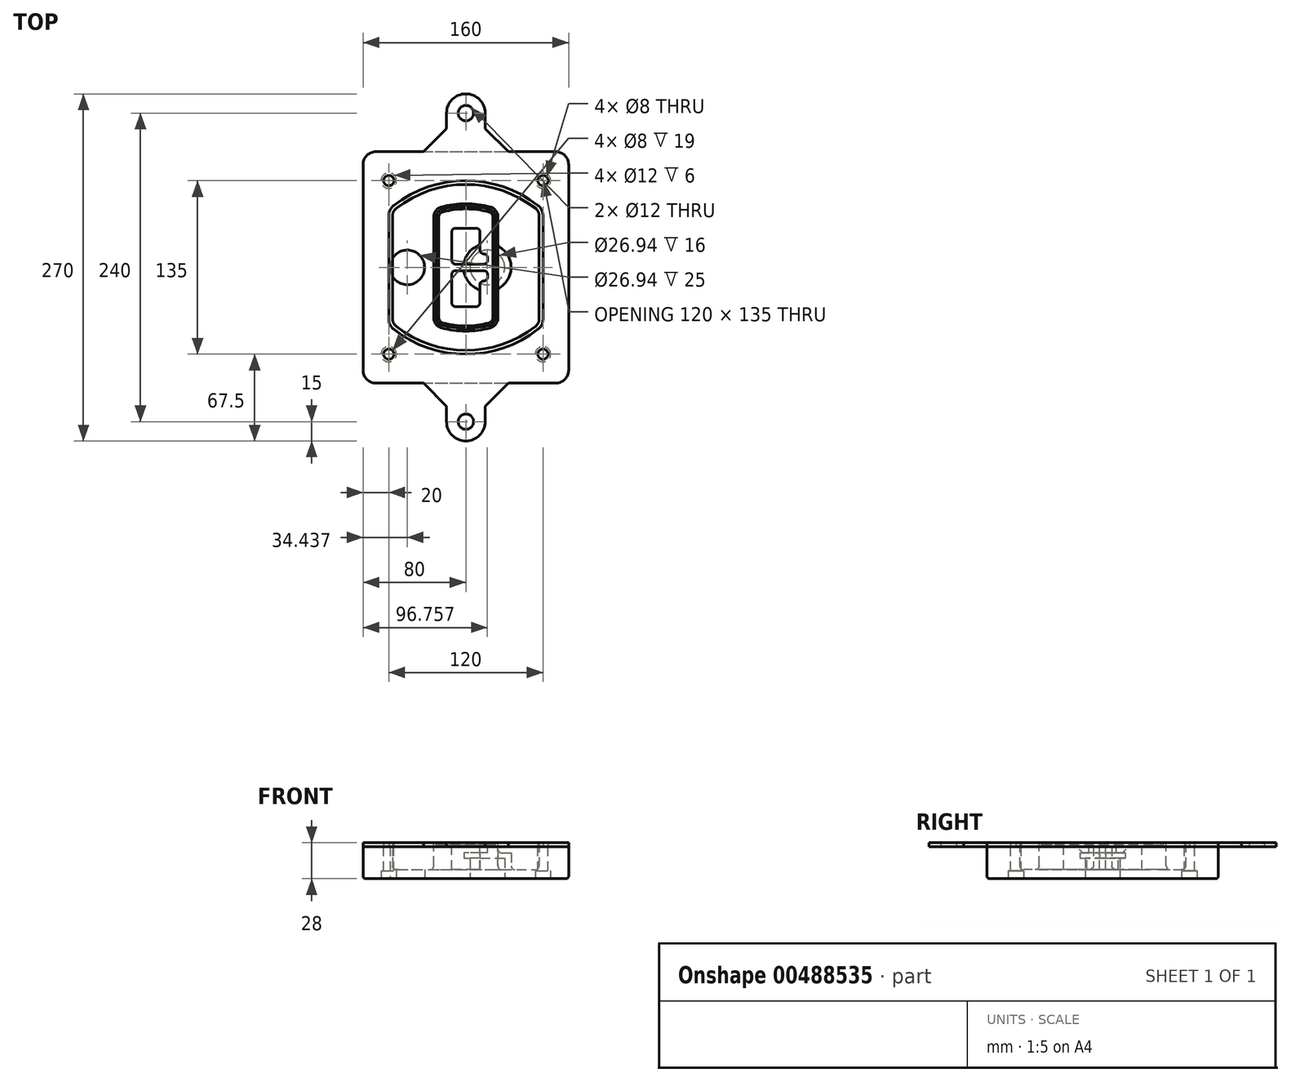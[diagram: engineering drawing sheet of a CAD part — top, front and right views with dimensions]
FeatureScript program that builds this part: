
annotation { "Feature Type Name" : "Feature", "Feature Type Description" : "" }
export const myFeature = defineFeature(function(context is Context, id is Id, definition is map)
    precondition{}
    {
        {
            var Q0;
            Q0=qCreatedBy(makeId("Top.planeOp"),FACE);
            var sketch = newSketch(context, id + "F0", { "sketchPlane" : qUnion([Q0])});
            skPoint(sketch, "E0.rect.middle", {"position": v(0, 0) * mm});
            skLineSegment(sketch, "E1.bottom", {"start": v(-70, -90) * mm, "end": v(70, -90) * mm});
            skLineSegment(sketch, "E1.top", {"start": v(-70, 90) * mm, "end": v(70, 90) * mm});
            skLineSegment(sketch, "E1.left", {"start": v(-80, -80) * mm, "end": v(-80, 80) * mm});
            skLineSegment(sketch, "E1.right", {"start": v(80, -80) * mm, "end": v(80, 80) * mm});
            skLineSegment(sketch, "E2", {"start": v(-80, 90) * mm, "end": v(80, -90) * mm, "construction": true});
            skLineSegment(sketch, "E3", {"start": v(80, 90) * mm, "end": v(-80, -90) * mm, "construction": true});
            skCircle(sketch, "E4", {"center": v(-60, 67.5) * mm, "radius": 4 * mm});
            skCircle(sketch, "E5", {"center": v(60, 67.5) * mm, "radius": 4 * mm});
            skCircle(sketch, "E6", {"center": v(60, -67.5) * mm, "radius": 4 * mm});
            skCircle(sketch, "E7", {"center": v(-60, -67.5) * mm, "radius": 4 * mm});
            skLineSegment(sketch, "E8", {"start": v(-60, 67.5) * mm, "end": v(60, 67.5) * mm, "construction": true});
            skLineSegment(sketch, "E9", {"start": v(60, 67.5) * mm, "end": v(60, -67.5) * mm, "construction": true});
            skLineSegment(sketch, "E10", {"start": v(60, -67.5) * mm, "end": v(-60, -67.5) * mm, "construction": true});
            skLineSegment(sketch, "E11", {"start": v(-60, -67.5) * mm, "end": v(-60, 67.5) * mm, "construction": true});
            skLineSegment(sketch, "E12", {"start": v(-60, 40.3) * mm, "end": v(-60, -40.3) * mm});
            skLineSegment(sketch, "E13", {"start": v(60, 40.3) * mm, "end": v(60, -40.3) * mm});
            skArc(sketch, "E14", {"start": v(56.15, 48.18) * mm, "mid": v(0, 67.5) * mm, "end": v(-56.15, 48.18) * mm});
            skArc(sketch, "E15", {"start": v(-56.15, -48.18) * mm, "mid": v(0, -67.5) * mm, "end": v(56.15, -48.18) * mm});
            skLineSegment(sketch, "E16", {"start": v(-60, 0) * mm, "end": v(60, 0) * mm, "construction": true});
            skPoint(sketch, "E17.visualSharp", {"position": v(-60, -45) * mm});
            skArc(sketch, "E17.filletArc", {"start": v(-60, -40.3) * mm, "mid": v(-58.99, -44.68) * mm, "end": v(-56.15, -48.18) * mm});
            skPoint(sketch, "E18.visualSharp", {"position": v(-60, 45) * mm});
            skArc(sketch, "E18.filletArc", {"start": v(-56.15, 48.18) * mm, "mid": v(-58.99, 44.68) * mm, "end": v(-60, 40.3) * mm});
            skPoint(sketch, "E19.visualSharp", {"position": v(60, 45) * mm});
            skArc(sketch, "E19.filletArc", {"start": v(60, 40.3) * mm, "mid": v(58.99, 44.68) * mm, "end": v(56.15, 48.18) * mm});
            skPoint(sketch, "E20.visualSharp", {"position": v(60, -45) * mm});
            skArc(sketch, "E20.filletArc", {"start": v(56.15, -48.18) * mm, "mid": v(58.99, -44.68) * mm, "end": v(60, -40.3) * mm});
            skPoint(sketch, "E21.visualSharp", {"position": v(-80, 90) * mm});
            skArc(sketch, "E21.filletArc", {"start": v(-70, 90) * mm, "mid": v(-77.07, 87.07) * mm, "end": v(-80, 80) * mm});
            skPoint(sketch, "E22.visualSharp", {"position": v(80, 90) * mm});
            skArc(sketch, "E22.filletArc", {"start": v(80, 80) * mm, "mid": v(77.07, 87.07) * mm, "end": v(70, 90) * mm});
            skPoint(sketch, "E23.visualSharp", {"position": v(80, -90) * mm});
            skArc(sketch, "E23.filletArc", {"start": v(70, -90) * mm, "mid": v(77.07, -87.07) * mm, "end": v(80, -80) * mm});
            skPoint(sketch, "E24.visualSharp", {"position": v(-80, -90) * mm});
            skArc(sketch, "E24.filletArc", {"start": v(-80, -80) * mm, "mid": v(-77.07, -87.07) * mm, "end": v(-70, -90) * mm});
            skArc(sketch, "E25.0", {"start": v(57, 40.3) * mm, "mid": v(56.3, 43.36) * mm, "end": v(54.3, 45.81) * mm});
            skLineSegment(sketch, "E25.1", {"start": v(57, 40.3) * mm, "end": v(57, -40.3) * mm});
            skArc(sketch, "E25.2", {"start": v(54.3, -45.81) * mm, "mid": v(56.3, -43.36) * mm, "end": v(57, -40.3) * mm});
            skArc(sketch, "E25.3", {"start": v(-54.3, -45.81) * mm, "mid": v(0, -64.5) * mm, "end": v(54.3, -45.81) * mm});
            skArc(sketch, "E25.4", {"start": v(-57, -40.3) * mm, "mid": v(-56.3, -43.36) * mm, "end": v(-54.3, -45.81) * mm});
            skArc(sketch, "E25.5", {"start": v(54.3, 45.81) * mm, "mid": v(0, 64.5) * mm, "end": v(-54.3, 45.81) * mm});
            skLineSegment(sketch, "E25.6", {"start": v(-57, 40.3) * mm, "end": v(-57, -40.3) * mm});
            skArc(sketch, "E25.7", {"start": v(-54.3, 45.81) * mm, "mid": v(-56.3, 43.36) * mm, "end": v(-57, 40.3) * mm});
            skArc(sketch, "E26.0", {"start": v(-58.62, 51.33) * mm, "mid": v(-62.58, 46.43) * mm, "end": v(-64, 40.3) * mm});
            skArc(sketch, "E26.1", {"start": v(58.62, 51.33) * mm, "mid": v(0, 71.5) * mm, "end": v(-58.62, 51.33) * mm});
            skArc(sketch, "E26.2", {"start": v(64, 40.3) * mm, "mid": v(62.58, 46.43) * mm, "end": v(58.62, 51.33) * mm});
            skLineSegment(sketch, "E26.3", {"start": v(64, 40.3) * mm, "end": v(64, -40.3) * mm});
            skArc(sketch, "E26.4", {"start": v(58.62, -51.33) * mm, "mid": v(62.58, -46.43) * mm, "end": v(64, -40.3) * mm});
            skLineSegment(sketch, "E26.5", {"start": v(-64, 40.3) * mm, "end": v(-64, -40.3) * mm});
            skArc(sketch, "E26.6", {"start": v(-58.62, -51.33) * mm, "mid": v(0, -71.5) * mm, "end": v(58.62, -51.33) * mm});
            skArc(sketch, "E26.7", {"start": v(-64, -40.3) * mm, "mid": v(-62.58, -46.43) * mm, "end": v(-58.62, -51.33) * mm});
            skSolve(sketch);
        }
        {
            var Q0;
            Q0=makeQuery(id+"F0.imprint","IMPRINT",FACE,{"disambiguationData":[TD([[makeQuery(id+"F0.imprint","IMPRINT",EDGE,{"derivedFrom":sQuery(id+"F0.wireOp",EDGE,"E1.bottom")}),1.0]])]});
            var Q1;
            Q1=makeQuery(id+"F0.imprint","IMPRINT",FACE,{"disambiguationData":[TD([[makeQuery(id+"F0.imprint","IMPRINT",EDGE,{"derivedFrom":sQuery(id+"F0.wireOp",EDGE,"E12")}),1.0]])]});
            var Q2;
            Q2=makeQuery(id+"F0.imprint","IMPRINT",FACE,{"disambiguationData":[TD([[makeQuery(id+"F0.imprint","IMPRINT",EDGE,{"derivedFrom":sQuery(id+"F0.wireOp",EDGE,"E25.0")}),1.0]])]});
            var Q3;
            Q3=makeQuery(id+"F0.imprint","IMPRINT",FACE,{"disambiguationData":[TD([[makeQuery(id+"F0.imprint","IMPRINT",EDGE,{"derivedFrom":sQuery(id+"F0.wireOp",EDGE,"E12")}),-1.0]])]});
            extrude(context, id + "F1", {"entities" : qUnion([Q0, Q1, Q2, Q3]), "oppositeDirection" : true, "depth" : 25 * mm});
        }
        {
            var Q0;
            Q0=makeQuery(id+"F0.imprint","IMPRINT",FACE,{"disambiguationData":[TD([[makeQuery(id+"F0.imprint","IMPRINT",EDGE,{"derivedFrom":sQuery(id+"F0.wireOp",EDGE,"E12")}),1.0]])]});
            extrude(context, id + "F2", {"entities" : qUnion([Q0]), "operationType" : NewBodyOperationType.ADD, "depth" : 3 * mm});
        }
        {
            var Q0;
            Q0=makeQuery(id+"F0.imprint","IMPRINT",FACE,{"disambiguationData":[TD([[makeQuery(id+"F0.imprint","IMPRINT",EDGE,{"derivedFrom":sQuery(id+"F0.wireOp",EDGE,"E25.0")}),1.0]])]});
            extrude(context, id + "F3", {"entities" : qUnion([Q0]), "operationType" : NewBodyOperationType.REMOVE, "oppositeDirection" : true, "depth" : 18 * mm});
        }
        {
            var Q0;
            Q0=makeQuery(id+"F2.opExtrude","CAP_FACE",FACE,{"disambiguationData":[OSD([sQuery(id+"F0.wireOp",EDGE,"E12"),sQuery(id+"F0.wireOp",EDGE,"E13"),sQuery(id+"F0.wireOp",EDGE,"E14"),sQuery(id+"F0.wireOp",EDGE,"E15"),sQuery(id+"F0.wireOp",EDGE,"E17.filletArc"),sQuery(id+"F0.wireOp",EDGE,"E18.filletArc"),sQuery(id+"F0.wireOp",EDGE,"E19.filletArc"),sQuery(id+"F0.wireOp",EDGE,"E20.filletArc"),sQuery(id+"F0.wireOp",EDGE,"E25.0"),sQuery(id+"F0.wireOp",EDGE,"E25.1"),sQuery(id+"F0.wireOp",EDGE,"E25.2"),sQuery(id+"F0.wireOp",EDGE,"E25.3"),sQuery(id+"F0.wireOp",EDGE,"E25.4"),sQuery(id+"F0.wireOp",EDGE,"E25.5"),sQuery(id+"F0.wireOp",EDGE,"E25.6"),sQuery(id+"F0.wireOp",EDGE,"E25.7")])],"isStart":false});
            var sketch = newSketch(context, id + "F4", { "sketchPlane" : qUnion([Q0])});
            skArc(sketch, "E27.0", {"start": v(-19.08, -46.97) * mm, "mid": v(0, -49.5) * mm, "end": v(19.08, -46.97) * mm});
            skArc(sketch, "E28.0", {"start": v(19.08, 46.97) * mm, "mid": v(0, 49.5) * mm, "end": v(-19.08, 46.97) * mm});
            skLineSegment(sketch, "E29", {"start": v(-25, 39.25) * mm, "end": v(-25, -39.25) * mm});
            skLineSegment(sketch, "E30", {"start": v(25, 39.25) * mm, "end": v(25, -39.25) * mm});
            skLineSegment(sketch, "E31", {"start": v(-25, 45.1) * mm, "end": v(25, 45.1) * mm, "construction": true});
            skLineSegment(sketch, "E32", {"start": v(-25, -45.1) * mm, "end": v(25, -45.1) * mm, "construction": true});
            skPoint(sketch, "E33.visualSharp", {"position": v(-25, 45.1) * mm});
            skArc(sketch, "E33.filletArc", {"start": v(-19.08, 46.97) * mm, "mid": v(-23.35, 44.11) * mm, "end": v(-25, 39.25) * mm});
            skPoint(sketch, "E34.visualSharp", {"position": v(25, 45.1) * mm});
            skArc(sketch, "E34.filletArc", {"start": v(25, 39.25) * mm, "mid": v(23.35, 44.11) * mm, "end": v(19.08, 46.97) * mm});
            skPoint(sketch, "E35.visualSharp", {"position": v(25, -45.1) * mm});
            skArc(sketch, "E35.filletArc", {"start": v(19.08, -46.97) * mm, "mid": v(23.35, -44.11) * mm, "end": v(25, -39.25) * mm});
            skPoint(sketch, "E36.visualSharp", {"position": v(-25, -45.1) * mm});
            skArc(sketch, "E36.filletArc", {"start": v(-25, -39.25) * mm, "mid": v(-23.35, -44.11) * mm, "end": v(-19.08, -46.97) * mm});
            skArc(sketch, "E37.0", {"start": v(54.3, 45.81) * mm, "mid": v(0, 64.5) * mm, "end": v(-54.3, 45.81) * mm});
            skArc(sketch, "E37.1", {"start": v(-54.3, 45.81) * mm, "mid": v(-56.3, 43.36) * mm, "end": v(-57, 40.3) * mm});
            skLineSegment(sketch, "E37.2", {"start": v(-57, 40.3) * mm, "end": v(-57, -40.3) * mm});
            skArc(sketch, "E37.3", {"start": v(-57, -40.3) * mm, "mid": v(-56.3, -43.36) * mm, "end": v(-54.3, -45.81) * mm});
            skArc(sketch, "E37.4", {"start": v(-54.3, -45.81) * mm, "mid": v(0, -64.5) * mm, "end": v(54.3, -45.81) * mm});
            skArc(sketch, "E37.5", {"start": v(54.3, -45.81) * mm, "mid": v(56.3, -43.36) * mm, "end": v(57, -40.3) * mm});
            skLineSegment(sketch, "E37.6", {"start": v(57, 40.3) * mm, "end": v(57, -40.3) * mm});
            skArc(sketch, "E37.7", {"start": v(57, 40.3) * mm, "mid": v(56.3, 43.36) * mm, "end": v(54.3, 45.81) * mm});
            skLineSegment(sketch, "E38.0", {"start": v(23, 39.25) * mm, "end": v(23, -39.25) * mm});
            skArc(sketch, "E38.1", {"start": v(18.56, -45.04) * mm, "mid": v(21.76, -42.9) * mm, "end": v(23, -39.25) * mm});
            skArc(sketch, "E38.2", {"start": v(-18.56, -45.04) * mm, "mid": v(0, -47.5) * mm, "end": v(18.56, -45.04) * mm});
            skArc(sketch, "E38.3", {"start": v(-23, -39.25) * mm, "mid": v(-21.76, -42.9) * mm, "end": v(-18.56, -45.04) * mm});
            skLineSegment(sketch, "E38.4", {"start": v(-23, 39.25) * mm, "end": v(-23, -39.25) * mm});
            skArc(sketch, "E38.5", {"start": v(23, 39.25) * mm, "mid": v(21.76, 42.9) * mm, "end": v(18.56, 45.04) * mm});
            skArc(sketch, "E38.6", {"start": v(-18.56, 45.04) * mm, "mid": v(-21.76, 42.9) * mm, "end": v(-23, 39.25) * mm});
            skArc(sketch, "E38.7", {"start": v(18.56, 45.04) * mm, "mid": v(0, 47.5) * mm, "end": v(-18.56, 45.04) * mm});
            skArc(sketch, "E39.0", {"start": v(21, 39.25) * mm, "mid": v(20.18, 41.68) * mm, "end": v(18.04, 43.1) * mm});
            skLineSegment(sketch, "E39.1", {"start": v(21, 39.25) * mm, "end": v(21, -39.25) * mm});
            skArc(sketch, "E39.2", {"start": v(18.04, -43.1) * mm, "mid": v(20.18, -41.68) * mm, "end": v(21, -39.25) * mm});
            skArc(sketch, "E39.3", {"start": v(-18.04, -43.1) * mm, "mid": v(0, -45.5) * mm, "end": v(18.04, -43.1) * mm});
            skArc(sketch, "E39.4", {"start": v(-21, -39.25) * mm, "mid": v(-20.18, -41.68) * mm, "end": v(-18.04, -43.1) * mm});
            skArc(sketch, "E39.5", {"start": v(18.04, 43.1) * mm, "mid": v(0, 45.5) * mm, "end": v(-18.04, 43.1) * mm});
            skLineSegment(sketch, "E39.6", {"start": v(-21, 39.25) * mm, "end": v(-21, -39.25) * mm});
            skArc(sketch, "E39.7", {"start": v(-18.04, 43.1) * mm, "mid": v(-20.18, 41.68) * mm, "end": v(-21, 39.25) * mm});
            skLineSegment(sketch, "E40", {"start": v(-25, 0) * mm, "end": v(25, 0) * mm, "construction": true});
            skLineSegment(sketch, "E41", {"start": v(-11, 5.5) * mm, "end": v(-11, 27.5) * mm});
            skLineSegment(sketch, "E42", {"start": v(-8, 30.5) * mm, "end": v(8, 30.5) * mm});
            skLineSegment(sketch, "E43", {"start": v(11, 27.5) * mm, "end": v(11, 13.5) * mm});
            skLineSegment(sketch, "E44", {"start": v(14, 10.5) * mm, "end": v(14, 10.5) * mm});
            skLineSegment(sketch, "E45", {"start": v(17, 7.5) * mm, "end": v(17, 5.5) * mm});
            skLineSegment(sketch, "E46", {"start": v(14, 2.5) * mm, "end": v(-8, 2.5) * mm});
            skPoint(sketch, "E47.visualSharp", {"position": v(-11, 30.5) * mm});
            skArc(sketch, "E47.filletArc", {"start": v(-8, 30.5) * mm, "mid": v(-10.12, 29.62) * mm, "end": v(-11, 27.5) * mm});
            skPoint(sketch, "E48.visualSharp", {"position": v(11, 30.5) * mm});
            skArc(sketch, "E48.filletArc", {"start": v(11, 27.5) * mm, "mid": v(10.12, 29.62) * mm, "end": v(8, 30.5) * mm});
            skPoint(sketch, "E49.visualSharp", {"position": v(11, 10.5) * mm});
            skArc(sketch, "E49.filletArc", {"start": v(11, 13.5) * mm, "mid": v(11.88, 11.38) * mm, "end": v(14, 10.5) * mm});
            skPoint(sketch, "E50.visualSharp", {"position": v(17, 10.5) * mm});
            skArc(sketch, "E50.filletArc", {"start": v(17, 7.5) * mm, "mid": v(16.12, 9.62) * mm, "end": v(14, 10.5) * mm});
            skPoint(sketch, "E51.visualSharp", {"position": v(17, 2.5) * mm});
            skArc(sketch, "E51.filletArc", {"start": v(14, 2.5) * mm, "mid": v(16.12, 3.38) * mm, "end": v(17, 5.5) * mm});
            skPoint(sketch, "E52.visualSharp", {"position": v(-11, 2.5) * mm});
            skArc(sketch, "E52.filletArc", {"start": v(-11, 5.5) * mm, "mid": v(-10.12, 3.38) * mm, "end": v(-8, 2.5) * mm});
            skLineSegment(sketch, "E53.0.MirrorCS", {"start": v(14, -2.5) * mm, "end": v(-8, -2.5) * mm});
            skArc(sketch, "E54.0.MirrorCS", {"start": v(-11, -5.5) * mm, "mid": v(-10.12, -3.38) * mm, "end": v(-8, -2.5) * mm});
            skLineSegment(sketch, "E55.0.MirrorCS", {"start": v(-11, -5.5) * mm, "end": v(-11, -27.5) * mm});
            skArc(sketch, "E56.0.MirrorCS", {"start": v(-8, -30.5) * mm, "mid": v(-10.12, -29.62) * mm, "end": v(-11, -27.5) * mm});
            skLineSegment(sketch, "E57.0.MirrorCS", {"start": v(-8, -30.5) * mm, "end": v(8, -30.5) * mm});
            skArc(sketch, "E58.0.MirrorCS", {"start": v(11, -27.5) * mm, "mid": v(10.12, -29.62) * mm, "end": v(8, -30.5) * mm});
            skLineSegment(sketch, "E59.0.MirrorCS", {"start": v(11, -27.5) * mm, "end": v(11, -13.5) * mm});
            skArc(sketch, "E60.0.MirrorCS", {"start": v(11, -13.5) * mm, "mid": v(11.88, -11.38) * mm, "end": v(14, -10.5) * mm});
            skArc(sketch, "E61.0.MirrorCS", {"start": v(17, -7.5) * mm, "mid": v(16.12, -9.62) * mm, "end": v(14, -10.5) * mm});
            skLineSegment(sketch, "E62.0.MirrorCS", {"start": v(17, -7.5) * mm, "end": v(17, -5.5) * mm});
            skArc(sketch, "E63.0.MirrorCS", {"start": v(14, -2.5) * mm, "mid": v(16.12, -3.38) * mm, "end": v(17, -5.5) * mm});
            skSolve(sketch);
        }
        {
            var Q0;
            Q0=makeQuery(id+"F4.imprint","IMPRINT",FACE,{"disambiguationData":[TD([[makeQuery(id+"F4.imprint","IMPRINT",EDGE,{"derivedFrom":sQuery(id+"F4.wireOp",EDGE,"E27.0")}),1.0]])]});
            var Q1;
            Q1=makeQuery(id+"F4.imprint","IMPRINT",FACE,{"disambiguationData":[TD([[makeQuery(id+"F4.imprint","IMPRINT",EDGE,{"derivedFrom":sQuery(id+"F4.wireOp",EDGE,"E38.0")}),-1.0]])]});
            var Q2;
            Q2=makeQuery(id+"F4.imprint","IMPRINT",FACE,{"disambiguationData":[TD([[makeQuery(id+"F4.imprint","IMPRINT",EDGE,{"derivedFrom":sQuery(id+"F4.wireOp",EDGE,"E39.0")}),1.0]])]});
            extrude(context, id + "F5", {"entities" : qUnion([Q0, Q1, Q2]), "operationType" : NewBodyOperationType.ADD, "endBound" : BoundingType.UP_TO_NEXT, "oppositeDirection" : true, "depth" : 25 * mm});
        }
        {
            var Q0;
            Q0=makeQuery(id+"F4.imprint","IMPRINT",FACE,{"disambiguationData":[TD([[makeQuery(id+"F4.imprint","IMPRINT",EDGE,{"derivedFrom":sQuery(id+"F4.wireOp",EDGE,"E38.0")}),-1.0]])]});
            extrude(context, id + "F6", {"entities" : qUnion([Q0]), "operationType" : NewBodyOperationType.REMOVE, "oppositeDirection" : true, "depth" : 2 * mm});
        }
        {
            var Q0;
            Q0=makeQuery(id+"F1.opExtrude","CAP_FACE",FACE,{"disambiguationData":[OSD([sQuery(id+"F0.wireOp",EDGE,"E1.bottom"),sQuery(id+"F0.wireOp",EDGE,"E1.top"),sQuery(id+"F0.wireOp",EDGE,"E1.left"),sQuery(id+"F0.wireOp",EDGE,"E1.right"),sQuery(id+"F0.wireOp",EDGE,"E4"),sQuery(id+"F0.wireOp",EDGE,"E5"),sQuery(id+"F0.wireOp",EDGE,"E6"),sQuery(id+"F0.wireOp",EDGE,"E7"),sQuery(id+"F0.wireOp",EDGE,"E21.filletArc"),sQuery(id+"F0.wireOp",EDGE,"E22.filletArc"),sQuery(id+"F0.wireOp",EDGE,"E23.filletArc"),sQuery(id+"F0.wireOp",EDGE,"E24.filletArc")])],"isStart":false});
            var sketch = newSketch(context, id + "F7", { "sketchPlane" : qUnion([Q0])});
            skCircle(sketch, "E64", {"center": v(16.76, 0) * mm, "radius": 13.47 * mm});
            skCircle(sketch, "E65", {"center": v(-45.56, 0) * mm, "radius": 13.47 * mm});
            skLineSegment(sketch, "E66", {"start": v(80, 0) * mm, "end": v(-80, 0) * mm});
            skCircle(sketch, "E67", {"center": v(16.76, 0) * mm, "radius": 18.47 * mm});
            skCircle(sketch, "E68", {"center": v(60, -67.5) * mm, "radius": 6 * mm});
            skCircle(sketch, "E69", {"center": v(-60, -67.5) * mm, "radius": 6 * mm});
            skCircle(sketch, "E70", {"center": v(-60, 67.5) * mm, "radius": 6 * mm});
            skCircle(sketch, "E71", {"center": v(60, 67.5) * mm, "radius": 6 * mm});
            skSolve(sketch);
        }
        {
            var Q0;
            {var subQ1=sQuery(id+"F7.wireOp",EDGE,"E66");var subQ4=sQuery(id+"F7.wireOp",EDGE,"E64");var subQ6=makeQuery(id+"F7.imprint","INTERSECT",VERTEX,{"disambiguationData":[OD(0.0)],"derivedFrom":[subQ4,subQ1]});Q0=makeQuery(id+"F7.imprint","IMPRINT",FACE,{"disambiguationData":[TD([[makeQuery(id+"F7.imprint","IMPRINT",EDGE,{"disambiguationData":[TD([[subQ6,-1.0]])],"derivedFrom":subQ4}),-1.0]])]});}
            var Q1;
            {var subQ0=sQuery(id+"F7.wireOp",EDGE,"E66");var subQ1=sQuery(id+"F7.wireOp",EDGE,"E64");var subQ3=makeQuery(id+"F7.imprint","INTERSECT",VERTEX,{"disambiguationData":[OD(0.0)],"derivedFrom":[subQ1,subQ0]});Q1=makeQuery(id+"F7.imprint","IMPRINT",FACE,{"disambiguationData":[TD([[makeQuery(id+"F7.imprint","IMPRINT",EDGE,{"disambiguationData":[TD([[subQ3,-1.0]])],"derivedFrom":subQ1}),1.0]])]});}
            var Q2;
            {var subQ0=sQuery(id+"F7.wireOp",EDGE,"E66");var subQ1=sQuery(id+"F7.wireOp",EDGE,"E64");var subQ3=makeQuery(id+"F7.imprint","INTERSECT",VERTEX,{"disambiguationData":[OD(0.0)],"derivedFrom":[subQ1,subQ0]});Q2=makeQuery(id+"F7.imprint","IMPRINT",FACE,{"disambiguationData":[TD([[makeQuery(id+"F7.imprint","IMPRINT",EDGE,{"disambiguationData":[TD([[subQ3,1.0]])],"derivedFrom":subQ1}),1.0]])]});}
            var Q3;
            {var subQ1=sQuery(id+"F7.wireOp",EDGE,"E66");var subQ4=sQuery(id+"F7.wireOp",EDGE,"E64");var subQ6=makeQuery(id+"F7.imprint","INTERSECT",VERTEX,{"disambiguationData":[OD(0.0)],"derivedFrom":[subQ4,subQ1]});Q3=makeQuery(id+"F7.imprint","IMPRINT",FACE,{"disambiguationData":[TD([[makeQuery(id+"F7.imprint","IMPRINT",EDGE,{"disambiguationData":[TD([[subQ6,1.0]])],"derivedFrom":subQ4}),-1.0]])]});}
            extrude(context, id + "F8", {"entities" : qUnion([Q0, Q1, Q2, Q3]), "operationType" : NewBodyOperationType.ADD, "oppositeDirection" : true, "depth" : 20 * mm});
        }
        {
            var Q0;
            {var subQ0=sQuery(id+"F7.wireOp",EDGE,"E66");var subQ1=sQuery(id+"F7.wireOp",EDGE,"E64");var subQ3=makeQuery(id+"F7.imprint","INTERSECT",VERTEX,{"disambiguationData":[OD(0.0)],"derivedFrom":[subQ1,subQ0]});Q0=makeQuery(id+"F7.imprint","IMPRINT",FACE,{"disambiguationData":[TD([[makeQuery(id+"F7.imprint","IMPRINT",EDGE,{"disambiguationData":[TD([[subQ3,-1.0]])],"derivedFrom":subQ1}),1.0]])]});}
            var Q1;
            {var subQ0=sQuery(id+"F7.wireOp",EDGE,"E66");var subQ1=sQuery(id+"F7.wireOp",EDGE,"E64");var subQ3=makeQuery(id+"F7.imprint","INTERSECT",VERTEX,{"disambiguationData":[OD(0.0)],"derivedFrom":[subQ1,subQ0]});Q1=makeQuery(id+"F7.imprint","IMPRINT",FACE,{"disambiguationData":[TD([[makeQuery(id+"F7.imprint","IMPRINT",EDGE,{"disambiguationData":[TD([[subQ3,1.0]])],"derivedFrom":subQ1}),1.0]])]});}
            extrude(context, id + "F9", {"entities" : qUnion([Q0, Q1]), "operationType" : NewBodyOperationType.REMOVE, "oppositeDirection" : true, "depth" : 16 * mm});
        }
        {
            var Q0;
            {var subQ0=sQuery(id+"F7.wireOp",EDGE,"E66");var subQ1=sQuery(id+"F7.wireOp",EDGE,"E65");var subQ3=makeQuery(id+"F7.imprint","INTERSECT",VERTEX,{"disambiguationData":[OD(0.0)],"derivedFrom":[subQ1,subQ0]});Q0=makeQuery(id+"F7.imprint","IMPRINT",FACE,{"disambiguationData":[TD([[makeQuery(id+"F7.imprint","IMPRINT",EDGE,{"disambiguationData":[TD([[subQ3,-1.0]])],"derivedFrom":subQ1}),1.0]])]});}
            var Q1;
            {var subQ0=sQuery(id+"F7.wireOp",EDGE,"E66");var subQ1=sQuery(id+"F7.wireOp",EDGE,"E65");var subQ3=makeQuery(id+"F7.imprint","INTERSECT",VERTEX,{"disambiguationData":[OD(0.0)],"derivedFrom":[subQ1,subQ0]});Q1=makeQuery(id+"F7.imprint","IMPRINT",FACE,{"disambiguationData":[TD([[makeQuery(id+"F7.imprint","IMPRINT",EDGE,{"disambiguationData":[TD([[subQ3,1.0]])],"derivedFrom":subQ1}),1.0]])]});}
            extrude(context, id + "F10", {"entities" : qUnion([Q0, Q1]), "operationType" : NewBodyOperationType.REMOVE, "oppositeDirection" : true, "depth" : 25 * mm});
        }
        {
            var Q0;
            Q0=makeQuery(id+"F7.imprint","IMPRINT",FACE,{"disambiguationData":[TD([[makeQuery(id+"F7.imprint","IMPRINT",EDGE,{"derivedFrom":sQuery(id+"F7.wireOp",EDGE,"E68")}),1.0]])]});
            var Q1;
            Q1=makeQuery(id+"F7.imprint","IMPRINT",FACE,{"disambiguationData":[TD([[makeQuery(id+"F7.imprint","IMPRINT",EDGE,{"derivedFrom":makeQuery(id+"F1.opExtrude","CAP_EDGE",EDGE,{"disambiguationData":[OSD([sQuery(id+"F0.wireOp",EDGE,"E5")])],"isStart":false})}),-1.0]])]});
            var Q2;
            Q2=makeQuery(id+"F7.imprint","IMPRINT",FACE,{"disambiguationData":[TD([[makeQuery(id+"F7.imprint","IMPRINT",EDGE,{"derivedFrom":sQuery(id+"F7.wireOp",EDGE,"E69")}),1.0]])]});
            var Q3;
            Q3=makeQuery(id+"F7.imprint","IMPRINT",FACE,{"disambiguationData":[TD([[makeQuery(id+"F7.imprint","IMPRINT",EDGE,{"derivedFrom":makeQuery(id+"F1.opExtrude","CAP_EDGE",EDGE,{"disambiguationData":[OSD([sQuery(id+"F0.wireOp",EDGE,"E4")])],"isStart":false})}),-1.0]])]});
            var Q4;
            Q4=makeQuery(id+"F7.imprint","IMPRINT",FACE,{"disambiguationData":[TD([[makeQuery(id+"F7.imprint","IMPRINT",EDGE,{"derivedFrom":sQuery(id+"F7.wireOp",EDGE,"E70")}),1.0]])]});
            var Q5;
            Q5=makeQuery(id+"F7.imprint","IMPRINT",FACE,{"disambiguationData":[TD([[makeQuery(id+"F7.imprint","IMPRINT",EDGE,{"derivedFrom":makeQuery(id+"F1.opExtrude","CAP_EDGE",EDGE,{"disambiguationData":[OSD([sQuery(id+"F0.wireOp",EDGE,"E7")])],"isStart":false})}),-1.0]])]});
            var Q6;
            Q6=makeQuery(id+"F7.imprint","IMPRINT",FACE,{"disambiguationData":[TD([[makeQuery(id+"F7.imprint","IMPRINT",EDGE,{"derivedFrom":sQuery(id+"F7.wireOp",EDGE,"E71")}),1.0]])]});
            var Q7;
            Q7=makeQuery(id+"F7.imprint","IMPRINT",FACE,{"disambiguationData":[TD([[makeQuery(id+"F7.imprint","IMPRINT",EDGE,{"derivedFrom":makeQuery(id+"F1.opExtrude","CAP_EDGE",EDGE,{"disambiguationData":[OSD([sQuery(id+"F0.wireOp",EDGE,"E6")])],"isStart":false})}),-1.0]])]});
            extrude(context, id + "F11", {"entities" : qUnion([Q0, Q1, Q2, Q3, Q4, Q5, Q6, Q7]), "operationType" : NewBodyOperationType.REMOVE, "oppositeDirection" : true, "depth" : 6 * mm});
        }
        {
            var Q0;
            Q0=makeQuery(id+"F9.boolean.opBoolean","COPY",FACE,{"derivedFrom":makeQuery(id+"F9.opExtrude","CAP_FACE",FACE,{"disambiguationData":[OSD([sQuery(id+"F7.wireOp",EDGE,"E64")])],"isStart":false})});
            var sketch = newSketch(context, id + "F12", { "sketchPlane" : qUnion([Q0])});
            skArc(sketch, "E72.0", {"start": v(11, 17.55) * mm, "mid": v(2.57, 11.82) * mm, "end": v(-1.54, 2.5) * mm});
            skArc(sketch, "E72.1", {"start": v(-1.54, -2.5) * mm, "mid": v(2.57, -11.82) * mm, "end": v(11, -17.55) * mm});
            skLineSegment(sketch, "E73", {"start": v(-1.54, -2.5) * mm, "end": v(14, -2.5) * mm});
            skLineSegment(sketch, "E74.0", {"start": v(14, 2.5) * mm, "end": v(-1.54, 2.5) * mm});
            skArc(sketch, "E74.1", {"start": v(14, 2.5) * mm, "mid": v(16.12, 3.38) * mm, "end": v(17, 5.5) * mm});
            skLineSegment(sketch, "E74.2", {"start": v(17, 7.5) * mm, "end": v(17, 5.5) * mm});
            skArc(sketch, "E74.3", {"start": v(17, 7.5) * mm, "mid": v(16.12, 9.62) * mm, "end": v(14, 10.5) * mm});
            skArc(sketch, "E74.4", {"start": v(11, 13.5) * mm, "mid": v(11.88, 11.38) * mm, "end": v(14, 10.5) * mm});
            skLineSegment(sketch, "E74.5", {"start": v(11, 17.55) * mm, "end": v(11, 13.5) * mm});
            skLineSegment(sketch, "E74.7", {"start": v(14, -2.5) * mm, "end": v(-1.54, -2.5) * mm});
            skArc(sketch, "E74.8", {"start": v(14, -2.5) * mm, "mid": v(16.12, -3.38) * mm, "end": v(17, -5.5) * mm});
            skLineSegment(sketch, "E74.9", {"start": v(17, -7.5) * mm, "end": v(17, -5.5) * mm});
            skArc(sketch, "E74.10", {"start": v(17, -7.5) * mm, "mid": v(16.12, -9.62) * mm, "end": v(14, -10.5) * mm});
            skArc(sketch, "E74.11", {"start": v(11, -13.5) * mm, "mid": v(11.88, -11.38) * mm, "end": v(14, -10.5) * mm});
            skLineSegment(sketch, "E74.12", {"start": v(11, -17.55) * mm, "end": v(11, -13.5) * mm});
            skPoint(sketch, "E75.orphan", {"position": v(11, -27.5) * mm});
            skPoint(sketch, "E76.orphan", {"position": v(-8, -2.5) * mm});
            skPoint(sketch, "E77.orphan", {"position": v(-8, 2.5) * mm});
            skPoint(sketch, "E78.orphan", {"position": v(11, 27.5) * mm});
            skSolve(sketch);
        }
        {
            var Q0;
            {var subQ7=sQuery(id+"F12.wireOp",EDGE,"E72.0");var subQ14=sQuery(id+"F12.wireOp",EDGE,"E72.1");var subQ16=sQuery(id+"F12.wireOp",EDGE,"E74.1");var subQ18=sQuery(id+"F12.wireOp",EDGE,"E74.8");Q0=qUnion([makeQuery(id+"F12.imprint","IMPRINT",FACE,{"disambiguationData":[TD([[makeQuery(id+"F12.imprint","IMPRINT",EDGE,{"derivedFrom":subQ7}),1.0]])]}),makeQuery(id+"F12.imprint","IMPRINT",FACE,{"disambiguationData":[TD([[makeQuery(id+"F12.imprint","IMPRINT",EDGE,{"derivedFrom":subQ14}),1.0]])]}),makeQuery(id+"F12.imprint","IMPRINT",FACE,{"disambiguationData":[TD([[makeQuery(id+"F12.imprint","IMPRINT",EDGE,{"derivedFrom":subQ16}),1.0]])]}),makeQuery(id+"F12.imprint","IMPRINT",FACE,{"disambiguationData":[TD([[makeQuery(id+"F12.imprint","IMPRINT",EDGE,{"derivedFrom":subQ18}),-1.0]])]})]);}
            var Q1;
            Q1=makeQuery(id+"F5.boolean.opBoolean","SPLIT",FACE,{"disambiguationData":[TD([makeQuery(id+"F5.opExtrude","SWEPT_FACE",FACE,{"disambiguationData":[OSD([sQuery(id+"F4.wireOp",EDGE,"E41")])]})])],"derivedFrom":makeQuery(id+"F3.boolean.opBoolean","COPY",FACE,{"derivedFrom":makeQuery(id+"F3.opExtrude","CAP_FACE",FACE,{"disambiguationData":[OSD([sQuery(id+"F0.wireOp",EDGE,"E25.0"),sQuery(id+"F0.wireOp",EDGE,"E25.1"),sQuery(id+"F0.wireOp",EDGE,"E25.2"),sQuery(id+"F0.wireOp",EDGE,"E25.3"),sQuery(id+"F0.wireOp",EDGE,"E25.4"),sQuery(id+"F0.wireOp",EDGE,"E25.5"),sQuery(id+"F0.wireOp",EDGE,"E25.6"),sQuery(id+"F0.wireOp",EDGE,"E25.7")])],"isStart":false})})});
            extrude(context, id + "F13", {"entities" : qUnion([Q0]), "operationType" : NewBodyOperationType.REMOVE, "endBound" : BoundingType.UP_TO_SURFACE, "endBoundEntityFace" : qUnion([Q1]), "depth" : 25 * mm});
        }
        {
            var Q0;
            Q0=makeQuery(id+"F3.boolean.opBoolean","COPY",EDGE,{"derivedFrom":makeQuery(id+"F3.opExtrude","CAP_EDGE",EDGE,{"disambiguationData":[OSD([sQuery(id+"F0.wireOp",EDGE,"E25.6")])],"isStart":false})});
            var Q1;
            Q1=makeQuery(id+"F8.boolean.opBoolean","INTERSECT",EDGE,{"derivedFrom":[makeQuery(id+"F5.opExtrude","SWEPT_FACE",FACE,{"disambiguationData":[OSD([sQuery(id+"F4.wireOp",EDGE,"E30")])]}),makeQuery(id+"F8.opExtrude","CAP_FACE",FACE,{"disambiguationData":[OSD([sQuery(id+"F7.wireOp",EDGE,"E67")])],"isStart":false})]});
            var Q2;
            Q2=makeQuery(id+"F8.boolean.opBoolean","INTERSECT",EDGE,{"disambiguationData":[OD(1.0)],"derivedFrom":[makeQuery(id+"F5.opExtrude","SWEPT_FACE",FACE,{"disambiguationData":[OSD([sQuery(id+"F4.wireOp",EDGE,"E30")])]}),makeQuery(id+"F8.opExtrude","SWEPT_FACE",FACE,{"disambiguationData":[OSD([sQuery(id+"F7.wireOp",EDGE,"E67")])]})]});
            var Q3;
            {var subQ0=sQuery(id+"F4.wireOp",EDGE,"E30");Q3=makeQuery(id+"F8.boolean.opBoolean","SPLIT",EDGE,{"disambiguationData":[TD([makeQuery(id+"F5.opExtrude","SWEPT_FACE",FACE,{"disambiguationData":[OSD([sQuery(id+"F4.wireOp",EDGE,"E35.filletArc")])]})])],"derivedFrom":makeQuery(id+"F5.opExtrude","CAP_EDGE",EDGE,{"disambiguationData":[OSD([subQ0])],"isStart":false})});}
            var Q4;
            {var subQ0=sQuery(id+"F0.wireOp",EDGE,"E25.7");var subQ1=sQuery(id+"F0.wireOp",EDGE,"E25.1");var subQ2=sQuery(id+"F0.wireOp",EDGE,"E25.6");var subQ3=sQuery(id+"F0.wireOp",EDGE,"E25.5");var subQ4=sQuery(id+"F0.wireOp",EDGE,"E25.4");var subQ5=sQuery(id+"F0.wireOp",EDGE,"E25.0");var subQ6=sQuery(id+"F0.wireOp",EDGE,"E25.2");var subQ7=sQuery(id+"F0.wireOp",EDGE,"E25.3");Q4=makeQuery(id+"F8.boolean.opBoolean","INTERSECT",EDGE,{"derivedFrom":[makeQuery(id+"F5.boolean.opBoolean","SPLIT",FACE,{"disambiguationData":[TD([makeQuery(id+"F2.opExtrude","SWEPT_FACE",FACE,{"disambiguationData":[OSD([subQ5])]})])],"derivedFrom":makeQuery(id+"F3.boolean.opBoolean","COPY",FACE,{"derivedFrom":makeQuery(id+"F3.opExtrude","CAP_FACE",FACE,{"disambiguationData":[OSD([subQ5,subQ1,subQ6,subQ7,subQ4,subQ3,subQ2,subQ0])],"isStart":false})})}),makeQuery(id+"F8.opExtrude","SWEPT_FACE",FACE,{"disambiguationData":[OSD([sQuery(id+"F7.wireOp",EDGE,"E67")])]})]});}
            var Q5;
            Q5=makeQuery(id+"F8.boolean.opBoolean","INTERSECT",EDGE,{"disambiguationData":[OD(0.0)],"derivedFrom":[makeQuery(id+"F5.opExtrude","SWEPT_FACE",FACE,{"disambiguationData":[OSD([sQuery(id+"F4.wireOp",EDGE,"E30")])]}),makeQuery(id+"F8.opExtrude","SWEPT_FACE",FACE,{"disambiguationData":[OSD([sQuery(id+"F7.wireOp",EDGE,"E67")])]})]});
            fillet(context, id + "F14", {"entities" : qUnion([Q0, Q1, Q2, Q3, Q4, Q5]), "radius" : 3 * mm, "tangentPropagation" : true, "allowEdgeOverflow" : false});
        }
        {
            var Q0;
            Q0=makeQuery(id+"F1.opExtrude","CAP_EDGE",EDGE,{"disambiguationData":[OSD([sQuery(id+"F0.wireOp",EDGE,"E1.bottom")])],"isStart":false});
            fillet(context, id + "F15", {"entities" : qUnion([Q0]), "radius" : 2 * mm, "tangentPropagation" : true, "allowEdgeOverflow" : false});
        }
        {
            var Q0;
            Q0=qCreatedBy(makeId("Top.planeOp"),FACE);
            var sketch = newSketch(context, id + "F16", { "sketchPlane" : qUnion([Q0])});
            skLineSegment(sketch, "E79", {"start": v(0, 90) * mm, "end": v(0, 120) * mm, "construction": true});
            skLineSegment(sketch, "E80", {"start": v(-33, 90) * mm, "end": v(-15, 108) * mm});
            skLineSegment(sketch, "E81", {"start": v(33, 90) * mm, "end": v(15, 108) * mm});
            skCircle(sketch, "E82", {"center": v(0, 120) * mm, "radius": 6 * mm});
            skArc(sketch, "E83", {"start": v(15, 120) * mm, "mid": v(0, 135) * mm, "end": v(-15, 120) * mm});
            skLineSegment(sketch, "E84", {"start": v(-15, 108) * mm, "end": v(-15, 120) * mm});
            skLineSegment(sketch, "E85", {"start": v(15, 108) * mm, "end": v(15, 120) * mm});
            skLineSegment(sketch, "E86", {"start": v(-80, 0) * mm, "end": v(80, 0) * mm, "construction": true});
            skLineSegment(sketch, "E87.MirrorCS", {"start": v(0, -90) * mm, "end": v(0, -120) * mm, "construction": true});
            skLineSegment(sketch, "E88.MirrorCS", {"start": v(33, -90) * mm, "end": v(15, -108) * mm});
            skCircle(sketch, "E89.MirrorC", {"center": v(0, -120) * mm, "radius": 6 * mm});
            skLineSegment(sketch, "E90.MirrorCS", {"start": v(15, -108) * mm, "end": v(15, -120) * mm});
            skLineSegment(sketch, "E91.MirrorCS", {"start": v(-15, -108) * mm, "end": v(-15, -120) * mm});
            skLineSegment(sketch, "E92.MirrorCS", {"start": v(-33, -90) * mm, "end": v(-15, -108) * mm});
            skArc(sketch, "E93.MirrorCS", {"start": v(15, -120) * mm, "mid": v(0, -135) * mm, "end": v(-15, -120) * mm});
            skLineSegment(sketch, "E94.0.0", {"start": v(70, 90) * mm, "end": v(-70, 90) * mm});
            skArc(sketch, "E94.0.1", {"start": v(-70, 90) * mm, "mid": v(-77.07, 87.07) * mm, "end": v(-80, 80) * mm});
            skLineSegment(sketch, "E94.0.2", {"start": v(-80, 80) * mm, "end": v(-80, -80) * mm});
            skArc(sketch, "E94.0.3", {"start": v(-80, -80) * mm, "mid": v(-77.07, -87.07) * mm, "end": v(-70, -90) * mm});
            skLineSegment(sketch, "E94.0.4", {"start": v(-70, -90) * mm, "end": v(70, -90) * mm});
            skArc(sketch, "E94.0.5", {"start": v(70, -90) * mm, "mid": v(77.07, -87.07) * mm, "end": v(80, -80) * mm});
            skLineSegment(sketch, "E94.0.6", {"start": v(80, -80) * mm, "end": v(80, 80) * mm});
            skArc(sketch, "E94.0.7", {"start": v(80, 80) * mm, "mid": v(77.07, 87.07) * mm, "end": v(70, 90) * mm});
            skLineSegment(sketch, "E95.0", {"start": v(-60, 40.3) * mm, "end": v(-60, -40.3) * mm});
            skArc(sketch, "E95.1", {"start": v(56.15, 48.18) * mm, "mid": v(0, 67.5) * mm, "end": v(-56.15, 48.18) * mm});
            skArc(sketch, "E95.2", {"start": v(-60, -40.3) * mm, "mid": v(-58.99, -44.68) * mm, "end": v(-56.15, -48.18) * mm});
            skArc(sketch, "E95.3", {"start": v(-56.15, -48.18) * mm, "mid": v(0, -67.5) * mm, "end": v(56.15, -48.18) * mm});
            skArc(sketch, "E95.4", {"start": v(56.15, -48.18) * mm, "mid": v(58.99, -44.68) * mm, "end": v(60, -40.3) * mm});
            skArc(sketch, "E95.5", {"start": v(-56.15, 48.18) * mm, "mid": v(-58.99, 44.68) * mm, "end": v(-60, 40.3) * mm});
            skLineSegment(sketch, "E95.6", {"start": v(60, 40.3) * mm, "end": v(60, -40.3) * mm});
            skArc(sketch, "E95.7", {"start": v(60, 40.3) * mm, "mid": v(58.99, 44.68) * mm, "end": v(56.15, 48.18) * mm});
            skCircle(sketch, "E96.0", {"center": v(-60, 67.5) * mm, "radius": 4 * mm});
            skCircle(sketch, "E96.1", {"center": v(60, 67.5) * mm, "radius": 4 * mm});
            skCircle(sketch, "E96.2", {"center": v(60, -67.5) * mm, "radius": 4 * mm});
            skCircle(sketch, "E96.3", {"center": v(-60, -67.5) * mm, "radius": 4 * mm});
            skSolve(sketch);
        }
        {
            var Q0;
            {var subQ1=sQuery(id+"F16.wireOp",EDGE,"E80");Q0=makeQuery(id+"F16.imprint","IMPRINT",FACE,{"disambiguationData":[TD([[makeQuery(id+"F16.imprint","IMPRINT",EDGE,{"derivedFrom":subQ1}),-1.0]])]});}
            var Q1;
            {var subQ1=sQuery(id+"F16.wireOp",EDGE,"E94.0.1");Q1=makeQuery(id+"F16.imprint","IMPRINT",FACE,{"disambiguationData":[TD([[makeQuery(id+"F16.imprint","IMPRINT",EDGE,{"derivedFrom":subQ1}),1.0]])]});}
            var Q2;
            {var subQ1=sQuery(id+"F16.wireOp",EDGE,"E92.MirrorCS");Q2=makeQuery(id+"F16.imprint","IMPRINT",FACE,{"disambiguationData":[TD([[makeQuery(id+"F16.imprint","IMPRINT",EDGE,{"derivedFrom":subQ1}),1.0]])]});}
            var Q3;
            Q3=makeQuery(id+"F2.opExtrude","CAP_FACE",FACE,{"disambiguationData":[OSD([sQuery(id+"F0.wireOp",EDGE,"E12"),sQuery(id+"F0.wireOp",EDGE,"E13"),sQuery(id+"F0.wireOp",EDGE,"E14"),sQuery(id+"F0.wireOp",EDGE,"E15"),sQuery(id+"F0.wireOp",EDGE,"E17.filletArc"),sQuery(id+"F0.wireOp",EDGE,"E18.filletArc"),sQuery(id+"F0.wireOp",EDGE,"E19.filletArc"),sQuery(id+"F0.wireOp",EDGE,"E20.filletArc"),sQuery(id+"F0.wireOp",EDGE,"E25.0"),sQuery(id+"F0.wireOp",EDGE,"E25.1"),sQuery(id+"F0.wireOp",EDGE,"E25.2"),sQuery(id+"F0.wireOp",EDGE,"E25.3"),sQuery(id+"F0.wireOp",EDGE,"E25.4"),sQuery(id+"F0.wireOp",EDGE,"E25.5"),sQuery(id+"F0.wireOp",EDGE,"E25.6"),sQuery(id+"F0.wireOp",EDGE,"E25.7")])],"isStart":false});
            extrude(context, id + "F17", {"entities" : qUnion([Q0, Q1, Q2]), "endBound" : BoundingType.UP_TO_SURFACE, "endBoundEntityFace" : qUnion([Q3]), "depth" : 25 * mm});
        }
    });
